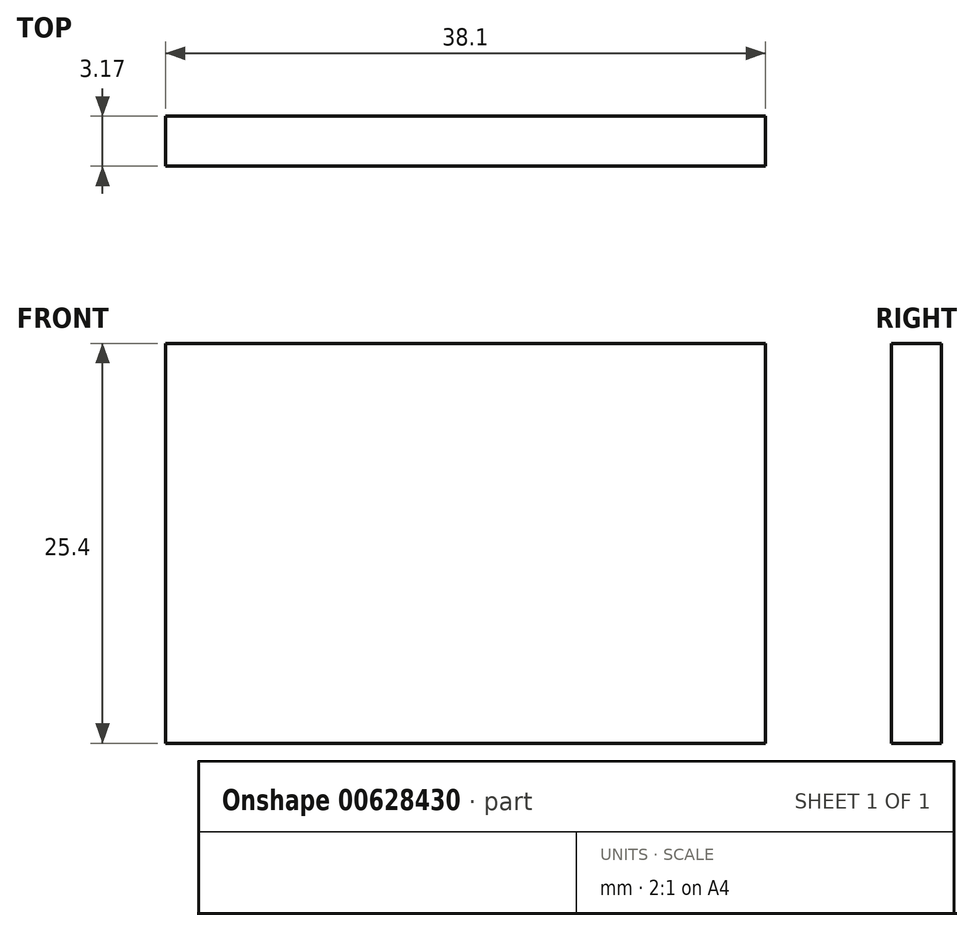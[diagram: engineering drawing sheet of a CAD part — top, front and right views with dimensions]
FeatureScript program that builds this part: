
annotation { "Feature Type Name" : "Feature", "Feature Type Description" : "" }
export const myFeature = defineFeature(function(context is Context, id is Id, definition is map)
    precondition{}
    {
        {
            var Q0;
            Q0=qCreatedBy(makeId("Top.planeOp"),FACE);
            var sketch = newSketch(context, id + "F0", { "sketchPlane" : qUnion([Q0])});
            skLineSegment(sketch, "E0.bottom", {"start": v(0, 0) * mm, "end": v(38.1, 0) * mm});
            skLineSegment(sketch, "E0.top", {"start": v(0, 3.17) * mm, "end": v(38.1, 3.17) * mm});
            skLineSegment(sketch, "E0.left", {"start": v(0, 0) * mm, "end": v(0, 3.17) * mm});
            skLineSegment(sketch, "E0.right", {"start": v(38.1, 0) * mm, "end": v(38.1, 3.17) * mm});
            skSolve(sketch);
        }
        {
            var Q0;
            Q0 = qSketchRegion(id + "F0", true);
            extrude(context, id + "F1", {"entities" : qUnion([Q0]), "depth" : 25.4 * mm, "offsetDistance" : 25.4 * mm});
        }
    });
